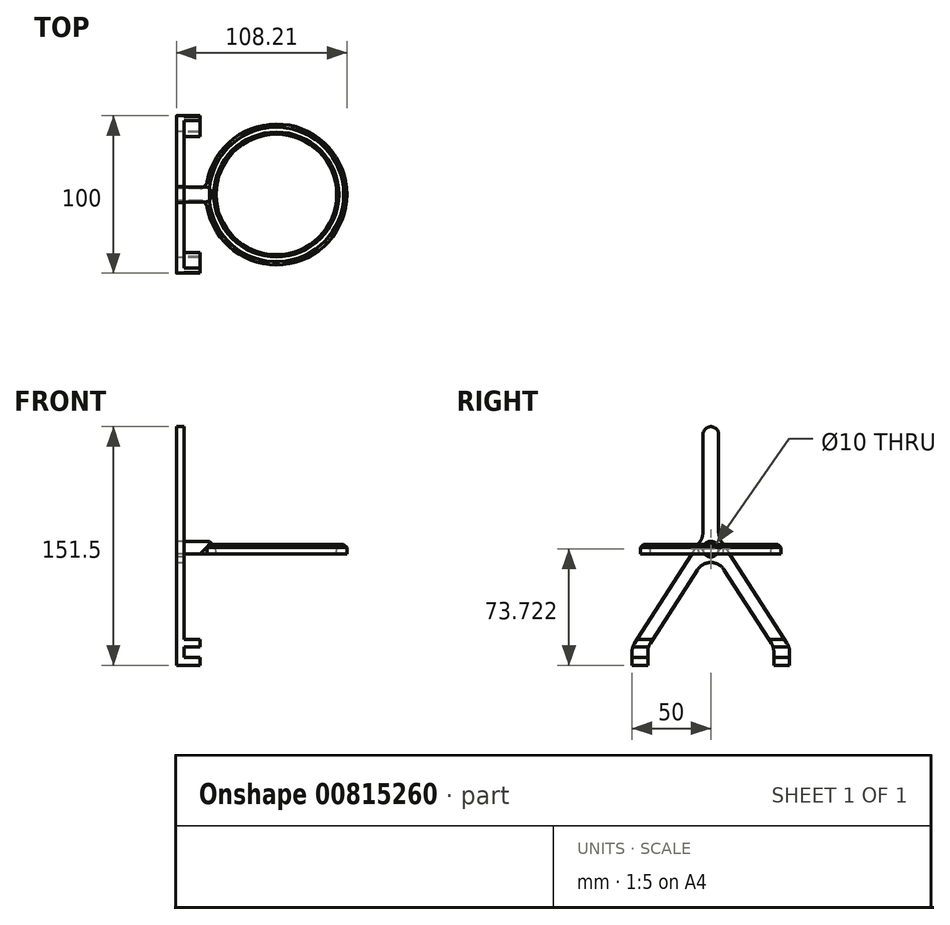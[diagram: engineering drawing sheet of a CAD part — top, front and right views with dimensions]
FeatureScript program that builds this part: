
annotation { "Feature Type Name" : "Feature", "Feature Type Description" : "" }
export const myFeature = defineFeature(function(context is Context, id is Id, definition is map)
    precondition{}
    {
        {
            var Q0;
            Q0=qCreatedBy(makeId("Right.planeOp"),FACE);
            cPlane(context, id + "F0", {"entities" : qUnion([Q0]), "cplaneType" : CPlaneType.OFFSET, "offset" : 70 * mm, "oppositeDirection" : true, "width" : 150 * mm, "height" : 150 * mm});
        }
        {
            var Q0;
            Q0=qCreatedBy(id+"F0.planeOp",FACE);
            var sketch = newSketch(context, id + "F1", { "sketchPlane" : qUnion([Q0])});
            skLineSegment(sketch, "E0", {"start": v(0, 62.22) * mm, "end": v(-40, 0) * mm});
            skLineSegment(sketch, "E1", {"start": v(-50, -11.5) * mm, "end": v(-50, 0) * mm});
            skLineSegment(sketch, "E2", {"start": v(-50, 0) * mm, "end": v(-5, 70) * mm});
            skLineSegment(sketch, "E3", {"start": v(-5, 70) * mm, "end": v(-5, 140) * mm});
            skLineSegment(sketch, "E4", {"start": v(-5, 140) * mm, "end": v(0, 140) * mm});
            skLineSegment(sketch, "E5", {"start": v(0, 140) * mm, "end": v(5, 140) * mm});
            skLineSegment(sketch, "E6", {"start": v(5, 140) * mm, "end": v(5, 70) * mm});
            skLineSegment(sketch, "E7", {"start": v(5, 70) * mm, "end": v(50, 0) * mm});
            skLineSegment(sketch, "E8", {"start": v(50, -11.5) * mm, "end": v(40, -11.5) * mm});
            skLineSegment(sketch, "E9", {"start": v(40, -11.5) * mm, "end": v(40, 0) * mm});
            skLineSegment(sketch, "E10", {"start": v(40, 0) * mm, "end": v(0, 62.22) * mm});
            skLineSegment(sketch, "E11", {"start": v(-50, -11.5) * mm, "end": v(-40, -11.5) * mm});
            skLineSegment(sketch, "E12", {"start": v(-40, -11.5) * mm, "end": v(-40, 0) * mm});
            skLineSegment(sketch, "E13", {"start": v(50, 0) * mm, "end": v(50, -11.5) * mm});
            skSolve(sketch);
        }
        {
            var Q0;
            Q0=makeQuery(id+"F1.imprint","IMPRINT",FACE,{"disambiguationData":[TD([[makeQuery(id+"F1.imprint","IMPRINT",EDGE,{"derivedFrom":sQuery(id+"F1.wireOp",EDGE,"E0")}),-1.0]])]});
            extrude(context, id + "F2", {"entities" : qUnion([Q0]), "depth" : 5 * mm, "offsetDistance" : 25 * mm});
        }
        {
            var Q0;
            Q0=makeQuery(id+"F2.opExtrude","SWEPT_EDGE",EDGE,{"disambiguationData":[OSD([sQuery(id+"F1.wireOp",EDGE,"E0"),sQuery(id+"F1.wireOp",EDGE,"2Qdq0gd9-1Wts-JzQb-aNDY-cJtiMOODCq13")])]});
            var Q1;
            Q1=makeQuery(id+"F2.opExtrude","SWEPT_EDGE",EDGE,{"disambiguationData":[OSD([sQuery(id+"F1.wireOp",EDGE,"E1"),sQuery(id+"F1.wireOp",EDGE,"E2")])]});
            var Q2;
            Q2=makeQuery(id+"F2.opExtrude","SWEPT_EDGE",EDGE,{"disambiguationData":[OSD([sQuery(id+"F1.wireOp",EDGE,"E9"),sQuery(id+"F1.wireOp",EDGE,"E10")])]});
            var Q3;
            Q3=makeQuery(id+"F2.opExtrude","SWEPT_EDGE",EDGE,{"disambiguationData":[OSD([sQuery(id+"F1.wireOp",EDGE,"E7"),sQuery(id+"F1.wireOp",EDGE,"AGq9xMHe-UfYn-AV5J-j3cz-IK4XJuOyjXgd")])]});
            var Q4;
            Q4=makeQuery(id+"F2.opExtrude","SWEPT_EDGE",EDGE,{"disambiguationData":[OSD([sQuery(id+"F1.wireOp",EDGE,"E0"),sQuery(id+"F1.wireOp",EDGE,"E10")])]});
            var Q5;
            Q5=makeQuery(id+"F2.opExtrude","SWEPT_EDGE",EDGE,{"disambiguationData":[OSD([sQuery(id+"F1.wireOp",EDGE,"E6"),sQuery(id+"F1.wireOp",EDGE,"E7")])]});
            var Q6;
            Q6=makeQuery(id+"F2.opExtrude","SWEPT_EDGE",EDGE,{"disambiguationData":[OSD([sQuery(id+"F1.wireOp",EDGE,"E2"),sQuery(id+"F1.wireOp",EDGE,"E3")])]});
            fillet(context, id + "F3", {"entities" : qUnion([Q0, Q1, Q2, Q3, Q4, Q5, Q6]), "radius" : 10 * mm, "tangentPropagation" : true, "allowEdgeOverflow" : false});
        }
        {
            var Q0;
            Q0=makeQuery(id+"F2.opExtrude","SWEPT_EDGE",EDGE,{"disambiguationData":[OSD([sQuery(id+"F1.wireOp",EDGE,"E3"),sQuery(id+"F1.wireOp",EDGE,"E4")])]});
            var Q1;
            Q1=makeQuery(id+"F2.opExtrude","SWEPT_EDGE",EDGE,{"disambiguationData":[OSD([sQuery(id+"F1.wireOp",EDGE,"E5"),sQuery(id+"F1.wireOp",EDGE,"E6")])]});
            fillet(context, id + "F4", {"entities" : qUnion([Q0, Q1]), "radius" : 5 * mm, "tangentPropagation" : true, "allowEdgeOverflow" : false});
        }
        {
            var Q0;
            Q0=makeQuery(id+"F2.opExtrude","CAP_FACE",FACE,{"disambiguationData":[OSD([sQuery(id+"F1.wireOp",EDGE,"E0"),sQuery(id+"F1.wireOp",EDGE,"2Qdq0gd9-1Wts-JzQb-aNDY-cJtiMOODCq13"),sQuery(id+"F1.wireOp",EDGE,"tQ7Qx2Js-TAmm-NFPa-ttCH-rFNCJ0qlS3tg"),sQuery(id+"F1.wireOp",EDGE,"E1"),sQuery(id+"F1.wireOp",EDGE,"E2"),sQuery(id+"F1.wireOp",EDGE,"E3"),sQuery(id+"F1.wireOp",EDGE,"E4"),sQuery(id+"F1.wireOp",EDGE,"E5"),sQuery(id+"F1.wireOp",EDGE,"E6"),sQuery(id+"F1.wireOp",EDGE,"E7"),sQuery(id+"F1.wireOp",EDGE,"AGq9xMHe-UfYn-AV5J-j3cz-IK4XJuOyjXgd"),sQuery(id+"F1.wireOp",EDGE,"E8"),sQuery(id+"F1.wireOp",EDGE,"E9"),sQuery(id+"F1.wireOp",EDGE,"E10")])],"isStart":false});
            var sketch = newSketch(context, id + "F5", { "sketchPlane" : qUnion([Q0])});
            skLineSegment(sketch, "E14.bottom", {"start": v(-50, -11.5) * mm, "end": v(-40, -11.5) * mm});
            skLineSegment(sketch, "E14.top", {"start": v(-50, -6.5) * mm, "end": v(-40, -6.5) * mm});
            skLineSegment(sketch, "E14.left", {"start": v(-50, -11.5) * mm, "end": v(-50, -6.5) * mm});
            skLineSegment(sketch, "E14.right", {"start": v(-40, -11.5) * mm, "end": v(-40, -6.5) * mm});
            skLineSegment(sketch, "E15", {"start": v(-49.56, 0) * mm, "end": v(-39.56, 0) * mm});
            skLineSegment(sketch, "E16", {"start": v(-46.79, 5) * mm, "end": v(-36.79, 5) * mm});
            skLineSegment(sketch, "E17", {"start": v(36.79, 5) * mm, "end": v(46.79, 5) * mm});
            skLineSegment(sketch, "E18", {"start": v(40, -6.5) * mm, "end": v(50, -6.5) * mm});
            skLineSegment(sketch, "E19", {"start": v(50, -6.5) * mm, "end": v(50, -11.5) * mm});
            skLineSegment(sketch, "E20", {"start": v(50, -11.5) * mm, "end": v(40, -11.5) * mm});
            skLineSegment(sketch, "E21", {"start": v(40, -11.5) * mm, "end": v(40, -6.5) * mm});
            skLineSegment(sketch, "E22", {"start": v(39.56, 0) * mm, "end": v(49.56, 0) * mm});
            skSolve(sketch);
        }
        {
            var Q0;
            Q0 = qSketchRegion(id + "F5", true);
            var Q1;
            {var subQ8=sQuery(id+"F5.wireOp",EDGE,"E15");Q1=makeQuery(id+"F5.imprint","IMPRINT",FACE,{"disambiguationData":[TD([[makeQuery(id+"F5.imprint","IMPRINT",EDGE,{"derivedFrom":subQ8}),1.0]])]});}
            var Q2;
            {var subQ12=sQuery(id+"F5.wireOp",EDGE,"E17");Q2=makeQuery(id+"F5.imprint","IMPRINT",FACE,{"disambiguationData":[TD([[makeQuery(id+"F5.imprint","IMPRINT",EDGE,{"derivedFrom":subQ12}),-1.0]])]});}
            extrude(context, id + "F6", {"entities" : qUnion([Q0, Q1, Q2]), "operationType" : NewBodyOperationType.ADD, "depth" : 10 * mm, "offsetDistance" : 25 * mm});
        }
        {
            var Q0;
            Q0=makeQuery(id+"F1.imprint","IMPRINT",FACE,{"disambiguationData":[TD([[makeQuery(id+"F1.imprint","IMPRINT",EDGE,{"derivedFrom":sQuery(id+"F1.wireOp",EDGE,"E0")}),-1.0]])]});
            var sketch = newSketch(context, id + "F7", { "sketchPlane" : qUnion([Q0])});
            skCircle(sketch, "E23", {"center": v(0, 62.22) * mm, "radius": 5 * mm});
            skSolve(sketch);
        }
        {
            var Q0;
            {var subQ0=sQuery(id+"F7.wireOp",EDGE,"E23");var subQ1=makeQuery(id+"F1.imprint","IMPRINT",EDGE,{"derivedFrom":sQuery(id+"F1.wireOp",EDGE,"E0")});var subQ2=makeQuery(id+"F7.imprint","INTERSECT",VERTEX,{"derivedFrom":[subQ1,subQ0]});Q0=makeQuery(id+"F7.imprint","IMPRINT",FACE,{"disambiguationData":[TD([[makeQuery(id+"F7.imprint","IMPRINT",EDGE,{"disambiguationData":[TD([[subQ2,1.0]])],"derivedFrom":subQ0}),1.0]])]});}
            var Q1;
            {var subQ0=sQuery(id+"F7.wireOp",EDGE,"E23");var subQ1=makeQuery(id+"F1.imprint","IMPRINT",EDGE,{"derivedFrom":sQuery(id+"F1.wireOp",EDGE,"E0")});var subQ2=makeQuery(id+"F7.imprint","INTERSECT",VERTEX,{"derivedFrom":[subQ1,subQ0]});Q1=makeQuery(id+"F7.imprint","IMPRINT",FACE,{"disambiguationData":[TD([[makeQuery(id+"F7.imprint","IMPRINT",EDGE,{"disambiguationData":[TD([[subQ2,-1.0]])],"derivedFrom":subQ0}),1.0]])]});}
            var Q2;
            Q2=sQuery(id+"F7.wireOp",EDGE,"E23");
            extrude(context, id + "F8", {"entities" : qUnion([Q0, Q1]), "operationType" : NewBodyOperationType.REMOVE, "surfaceEntities" : qUnion([Q2]), "endBound" : BoundingType.UP_TO_NEXT, "depth" : 25 * mm, "offsetDistance" : 25 * mm});
        }
        {
            var Q0;
            Q0=qCreatedBy(makeId("Top.planeOp"),FACE);
            var Q1;
            Q1=sQuery(id+"F1.wireOp",VERTEX,"E0.start");
            cPlane(context, id + "F9", {"entities" : qUnion([Q0, Q1]), "cplaneType" : CPlaneType.PLANE_POINT, "offset" : 25 * mm, "width" : 150 * mm, "height" : 150 * mm});
        }
        {
            var Q0;
            Q0=qCreatedBy(id+"F9.planeOp",FACE);
            var sketch = newSketch(context, id + "F10", { "sketchPlane" : qUnion([Q0])});
            skLineSegment(sketch, "E24", {"start": v(-70, 0) * mm, "end": v(-45, 0) * mm, "construction": true});
            skCircle(sketch, "E25", {"center": v(-6.5, 0) * mm, "radius": 38.5 * mm});
            skPoint(sketch, "E26", {"position": v(-6.5, -38.5) * mm});
            skSolve(sketch);
        }
        {
            var Q0;
            Q0=qCreatedBy(makeId("Right.planeOp"),FACE);
            var Q1;
            Q1=sQuery(id+"F10.wireOp",VERTEX,"E25.center");
            cPlane(context, id + "F11", {"entities" : qUnion([Q0, Q1]), "cplaneType" : CPlaneType.PLANE_POINT, "offset" : 25 * mm, "width" : 150 * mm, "height" : 150 * mm});
        }
        {
            var Q0;
            Q0=qCreatedBy(id+"F11.planeOp",FACE);
            var sketch = newSketch(context, id + "F12", { "sketchPlane" : qUnion([Q0])});
            skLineSegment(sketch, "E27", {"start": v(-38.7, 65.22) * mm, "end": v(-38.3, 59.22) * mm});
            skLineSegment(sketch, "E28", {"start": v(-38.3, 59.22) * mm, "end": v(-44.7, 59.22) * mm});
            skLineSegment(sketch, "E29", {"start": v(-44.7, 59.22) * mm, "end": v(-44.7, 65.22) * mm});
            skLineSegment(sketch, "E30", {"start": v(-44.7, 65.22) * mm, "end": v(-38.7, 65.22) * mm});
            skLineSegment(sketch, "E31", {"start": v(-38.7, 65.22) * mm, "end": v(-38.7, 59.22) * mm, "construction": true});
            skSolve(sketch);
        }
        {
            var Q0;
            Q0=makeQuery(id+"F12.imprint","IMPRINT",FACE,{"disambiguationData":[TD([[makeQuery(id+"F12.imprint","IMPRINT",EDGE,{"derivedFrom":sQuery(id+"F12.wireOp",EDGE,"E27")}),-1.0]])]});
            var Q1;
            Q1=sQuery(id+"F10.wireOp",EDGE,"E25");
            sweep(context, id + "F13", {"profiles" : qUnion([Q0]), "path" : qUnion([Q1])});
        }
        {
            var Q0;
            Q0=makeQuery(id+"F1.imprint","IMPRINT",FACE,{"disambiguationData":[TD([[makeQuery(id+"F1.imprint","IMPRINT",EDGE,{"derivedFrom":sQuery(id+"F1.wireOp",EDGE,"E0")}),-1.0]])]});
            var sketch = newSketch(context, id + "F14", { "sketchPlane" : qUnion([Q0])});
            skArc(sketch, "E32", {"start": v(3.75, 59.22) * mm, "mid": v(0, 67.02) * mm, "end": v(-3.75, 59.22) * mm});
            skLineSegment(sketch, "E33", {"start": v(3.75, 59.22) * mm, "end": v(-3.75, 59.22) * mm});
            skSolve(sketch);
        }
        {
            var Q0;
            Q0 = qSketchRegion(id + "F14", true);
            extrude(context, id + "F15", {"entities" : qUnion([Q0]), "operationType" : NewBodyOperationType.ADD, "depth" : 22.5 * mm, "offsetDistance" : 25 * mm});
        }
        {
            var Q0;
            Q0=makeQuery(id+"F15.opExtrude","CAP_EDGE",EDGE,{"disambiguationData":[OSD([sQuery(id+"F14.wireOp",EDGE,"E32")])],"isStart":false});
            chamfer(context, id + "F16", {"entities" : qUnion([Q0]), "width" : 1.5 * mm, "tangentPropagation" : true});
        }
        {
            var Q0;
            Q0=makeQuery(id+"F13.opSweep","SWEPT_EDGE",EDGE,{"disambiguationData":[OSD([sQuery(id+"F10.wireOp",EDGE,"E25"),sQuery(id+"F12.wireOp",EDGE,"E29"),sQuery(id+"F12.wireOp",EDGE,"E30")])]});
            chamfer(context, id + "F17", {"entities" : qUnion([Q0]), "width" : 2 * mm, "tangentPropagation" : true});
        }
        {
            var Q0;
            Q0=makeQuery(id+"F13.opSweep","SWEPT_EDGE",EDGE,{"disambiguationData":[OSD([sQuery(id+"F10.wireOp",EDGE,"E25"),sQuery(id+"F12.wireOp",EDGE,"E27"),sQuery(id+"F12.wireOp",EDGE,"E30")])]});
            chamfer(context, id + "F18", {"entities" : qUnion([Q0]), "width" : 1 * mm, "tangentPropagation" : true});
        }
        {
            var Q0;
            Q0=makeQuery(id+"F15.boolean.opBoolean","INTERSECT",EDGE,{"disambiguationData":[OD(1.0)],"derivedFrom":[makeQuery(id+"F13.opSweep","SWEPT_FACE",FACE,{"disambiguationData":[OSD([sQuery(id+"F10.wireOp",EDGE,"E25"),sQuery(id+"F12.wireOp",EDGE,"E29")])]}),makeQuery(id+"F15.opExtrude","SWEPT_FACE",FACE,{"disambiguationData":[OSD([sQuery(id+"F14.wireOp",EDGE,"E32")])]})]});
            var Q1;
            Q1=makeQuery(id+"F15.boolean.opBoolean","INTERSECT",EDGE,{"disambiguationData":[OD(0.0)],"derivedFrom":[makeQuery(id+"F13.opSweep","SWEPT_FACE",FACE,{"disambiguationData":[OSD([sQuery(id+"F10.wireOp",EDGE,"E25"),sQuery(id+"F12.wireOp",EDGE,"E29")])]}),makeQuery(id+"F15.opExtrude","SWEPT_FACE",FACE,{"disambiguationData":[OSD([sQuery(id+"F14.wireOp",EDGE,"E32")])]})]});
            fillet(context, id + "F19", {"entities" : qUnion([Q0, Q1]), "radius" : 4 * mm, "tangentPropagation" : true, "allowEdgeOverflow" : false});
        }
    });
